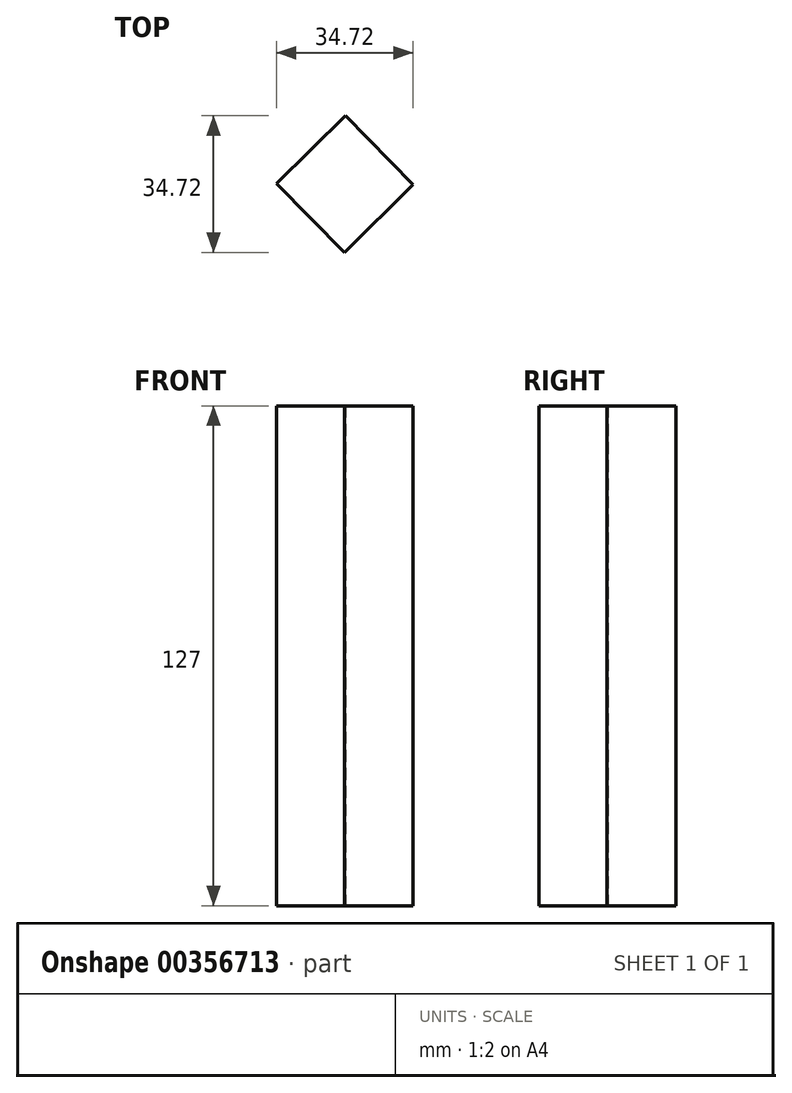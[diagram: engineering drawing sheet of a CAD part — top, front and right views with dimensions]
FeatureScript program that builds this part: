
annotation { "Feature Type Name" : "Feature", "Feature Type Description" : "" }
export const myFeature = defineFeature(function(context is Context, id is Id, definition is map)
    precondition{}
    {
        {
            var Q0;
            Q0=qCreatedBy(makeId("Top.planeOp"),FACE);
            var sketch = newSketch(context, id + "F0", { "sketchPlane" : qUnion([Q0])});
            skCircle(sketch, "E0.cCircle", {"center": v(0, 0) * mm, "radius": 12.28 * mm, "construction": true});
            skLineSegment(sketch, "E0.0", {"start": v(17.36, -0.12) * mm, "end": v(-0.12, -17.36) * mm});
            skLineSegment(sketch, "E0.1", {"start": v(-0.12, -17.36) * mm, "end": v(-17.36, 0.12) * mm});
            skLineSegment(sketch, "E0.2", {"start": v(-17.36, 0.12) * mm, "end": v(0.12, 17.36) * mm});
            skLineSegment(sketch, "E0.3", {"start": v(0.12, 17.36) * mm, "end": v(17.36, -0.12) * mm});
            skPoint(sketch, "E0.0.midPoint", {"position": v(8.62, -8.74) * mm});
            skSolve(sketch);
        }
        {
            var Q0;
            Q0 = qSketchRegion(id + "F0", true);
            extrude(context, id + "F1", {"entities" : qUnion([Q0]), "depth" : 127 * mm});
        }
    });
